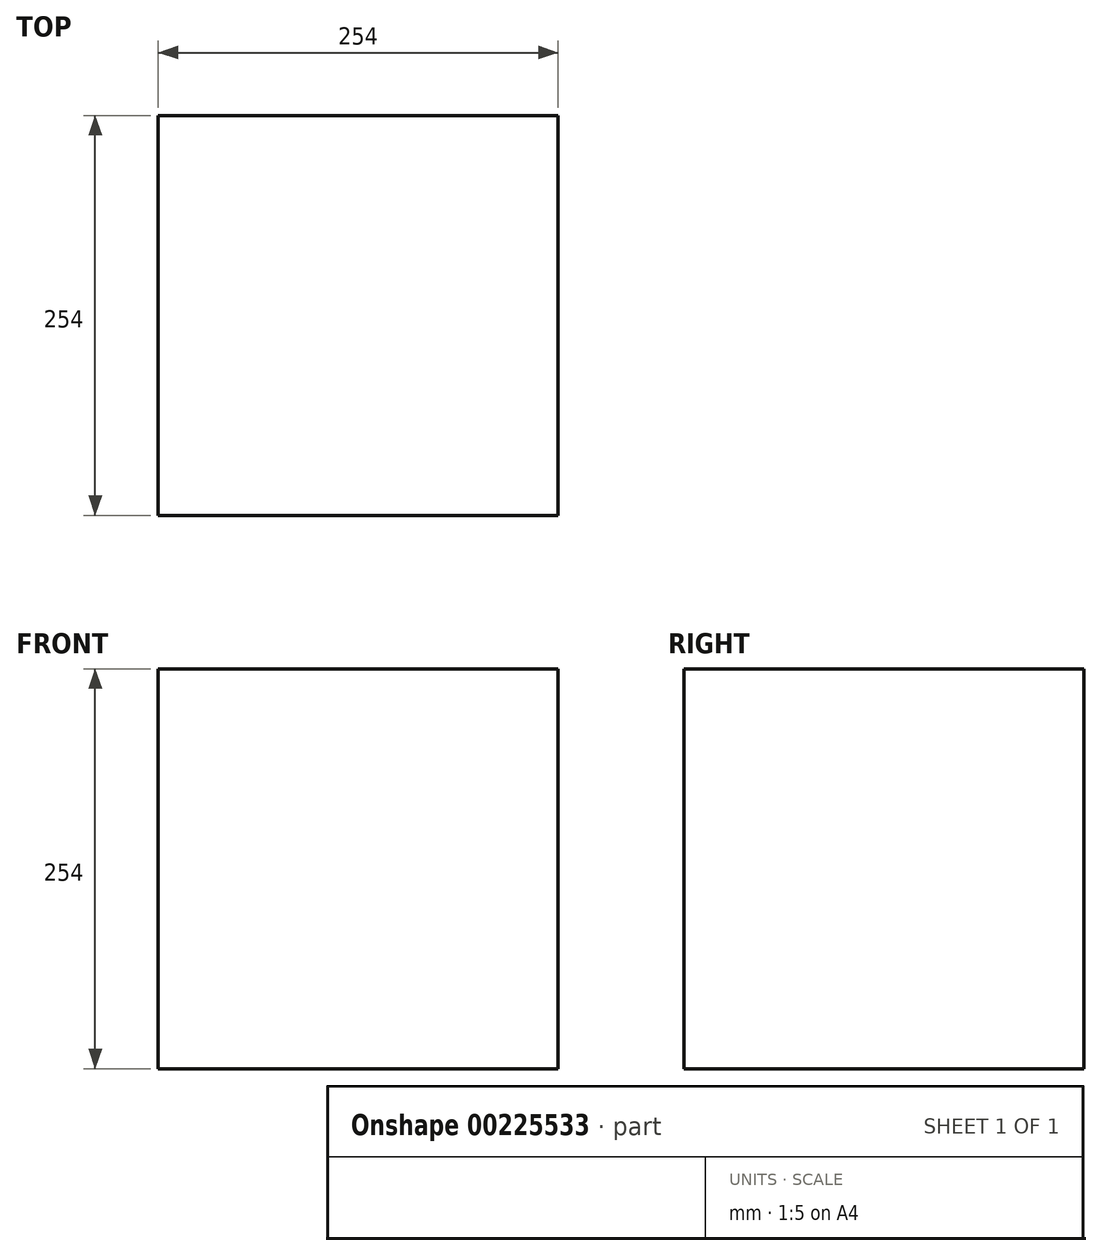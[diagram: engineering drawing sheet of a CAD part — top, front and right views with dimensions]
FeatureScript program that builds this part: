
annotation { "Feature Type Name" : "Feature", "Feature Type Description" : "" }
export const myFeature = defineFeature(function(context is Context, id is Id, definition is map)
    precondition{}
    {
        {
            var Q0;
            Q0=qCreatedBy(makeId("Front.planeOp"),FACE);
            var sketch = newSketch(context, id + "F0", { "sketchPlane" : qUnion([Q0])});
            skLineSegment(sketch, "E0.bottom", {"start": v(-138.3, 206.68) * mm, "end": v(115.7, 206.68) * mm});
            skLineSegment(sketch, "E0.top", {"start": v(-138.3, -47.32) * mm, "end": v(115.7, -47.32) * mm});
            skLineSegment(sketch, "E0.left", {"start": v(-138.3, 206.68) * mm, "end": v(-138.3, -47.32) * mm});
            skLineSegment(sketch, "E0.right", {"start": v(115.7, 206.68) * mm, "end": v(115.7, -47.32) * mm});
            skSolve(sketch);
        }
        {
            var Q0;
            Q0=makeQuery(id+"F0.imprint","IMPRINT",FACE,{"disambiguationData":[TD([[makeQuery(id+"F0.imprint","IMPRINT",EDGE,{"derivedFrom":sQuery(id+"F0.wireOp",EDGE,"E0.bottom")}),-1.0]])]});
            extrude(context, id + "F1", {"entities" : qUnion([Q0]), "depth" : 254 * mm});
        }
    });
